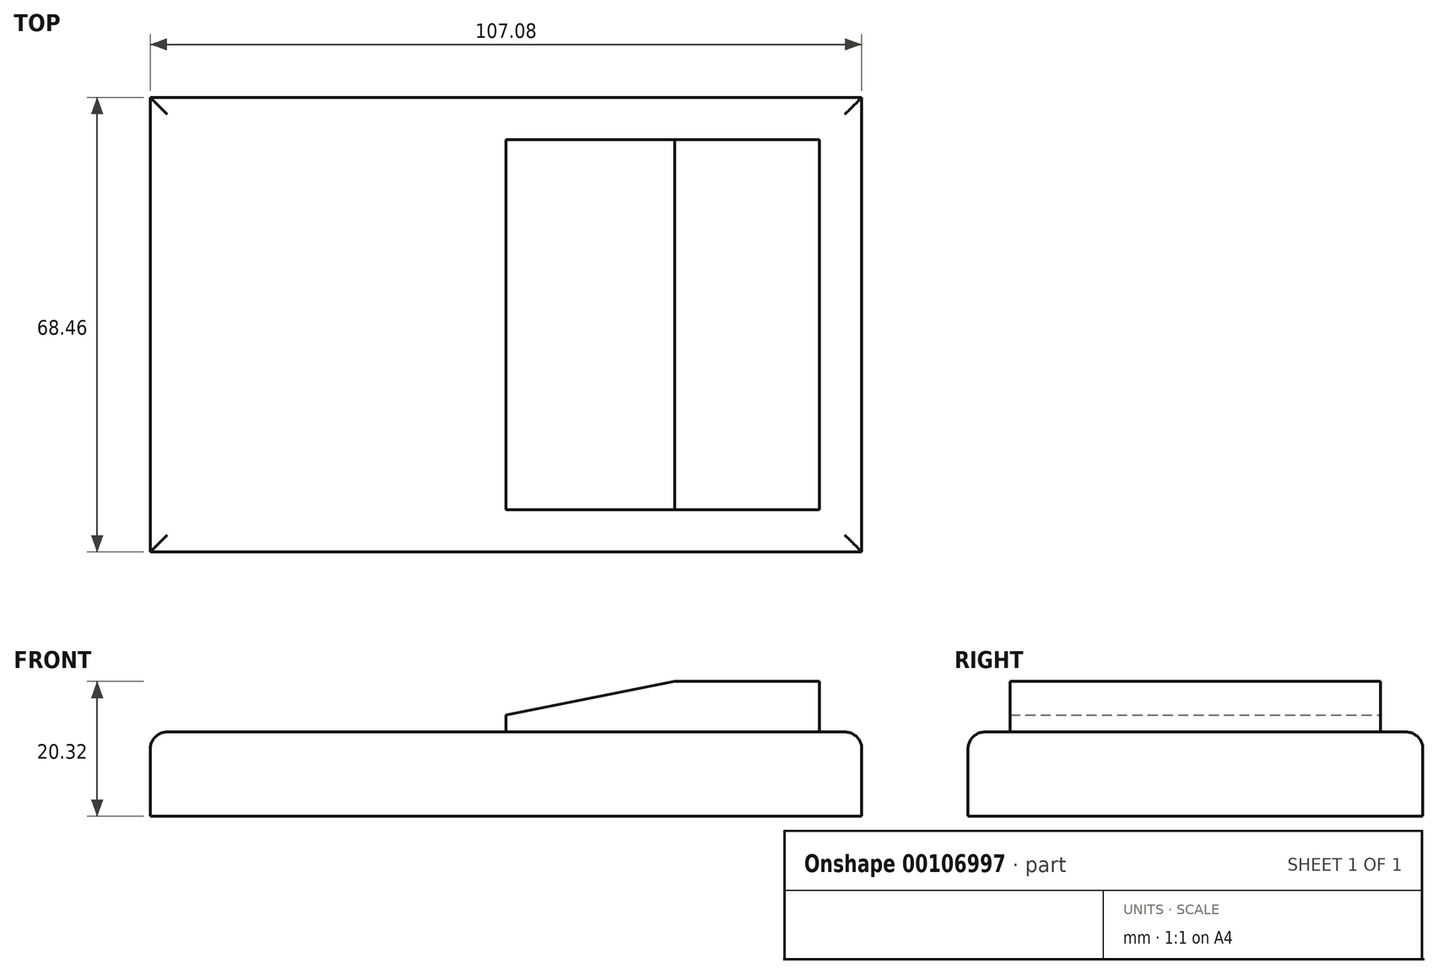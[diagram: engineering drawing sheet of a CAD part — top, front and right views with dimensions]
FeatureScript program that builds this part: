
annotation { "Feature Type Name" : "Feature", "Feature Type Description" : "" }
export const myFeature = defineFeature(function(context is Context, id is Id, definition is map)
    precondition{}
    {
        {
            var Q0;
            Q0=qCreatedBy(makeId("Top.planeOp"),FACE);
            var sketch = newSketch(context, id + "F0", { "sketchPlane" : qUnion([Q0])});
            skLineSegment(sketch, "E0.bottom", {"start": v(53.54, -34.23) * mm, "end": v(-53.54, -34.23) * mm});
            skLineSegment(sketch, "E0.top", {"start": v(53.54, 34.23) * mm, "end": v(-53.54, 34.23) * mm});
            skLineSegment(sketch, "E0.left", {"start": v(53.54, -34.23) * mm, "end": v(53.54, 34.23) * mm});
            skLineSegment(sketch, "E0.right", {"start": v(-53.54, -34.23) * mm, "end": v(-53.54, 34.23) * mm});
            skPoint(sketch, "E0.middle", {"position": v(0, 0) * mm});
            skSolve(sketch);
        }
        {
            var Q0;
            Q0=qCreatedBy(makeId("Top.planeOp"),FACE);
            var sketch = newSketch(context, id + "F1", { "sketchPlane" : qUnion([Q0])});
            skLineSegment(sketch, "E1.bottom", {"start": v(0, 27.88) * mm, "end": v(47.2, 27.88) * mm});
            skLineSegment(sketch, "E1.top", {"start": v(0, -27.88) * mm, "end": v(47.2, -27.88) * mm});
            skLineSegment(sketch, "E1.left", {"start": v(0, 27.88) * mm, "end": v(0, -27.88) * mm});
            skLineSegment(sketch, "E1.right", {"start": v(47.2, 27.88) * mm, "end": v(47.2, -27.88) * mm});
            skSolve(sketch);
        }
        {
            var Q0;
            Q0 = qSketchRegion(id + "F0", true);
            extrude(context, id + "F2", {"entities" : qUnion([Q0]), "depth" : 12.7 * mm});
        }
        {
            var Q0;
            Q0=makeQuery(id+"F1.imprint","IMPRINT",FACE,{"disambiguationData":[TD([[makeQuery(id+"F1.imprint","IMPRINT",EDGE,{"derivedFrom":sQuery(id+"F1.wireOp",EDGE,"E1.bottom")}),-1.0]])]});
            extrude(context, id + "F3", {"entities" : qUnion([Q0]), "operationType" : NewBodyOperationType.ADD, "depth" : 20.32 * mm});
        }
        {
            var Q0;
            Q0=makeQuery(id+"F3.opExtrude","CAP_EDGE",EDGE,{"disambiguationData":[OSD([sQuery(id+"F1.wireOp",EDGE,"E1.left")])],"isStart":false});
            chamfer(context, id + "F4", {"entities" : qUnion([Q0]), "chamferType" : ChamferType.TWO_OFFSETS, "width1" : 25.4 * mm, "oppositeDirection" : false, "width2" : 5.08 * mm});
        }
        {
            var Q0;
            Q0=makeQuery(id+"F2.opExtrude","CAP_EDGE",EDGE,{"disambiguationData":[OSD([sQuery(id+"F0.wireOp",EDGE,"E0.top")])],"isStart":false});
            var Q1;
            Q1=makeQuery(id+"F2.opExtrude","CAP_EDGE",EDGE,{"disambiguationData":[OSD([sQuery(id+"F0.wireOp",EDGE,"E0.left")])],"isStart":false});
            var Q2;
            Q2=makeQuery(id+"F2.opExtrude","CAP_EDGE",EDGE,{"disambiguationData":[OSD([sQuery(id+"F0.wireOp",EDGE,"E0.bottom")])],"isStart":false});
            var Q3;
            Q3=makeQuery(id+"F2.opExtrude","CAP_EDGE",EDGE,{"disambiguationData":[OSD([sQuery(id+"F0.wireOp",EDGE,"E0.right")])],"isStart":false});
            fillet(context, id + "F5", {"entities" : qUnion([Q0, Q1, Q2, Q3]), "radius" : 2.54 * mm, "tangentPropagation" : true, "allowEdgeOverflow" : false});
        }
    });
